# Revit family: Shower-Whitehall-BestCare-WH418-CSH
name_source: partatom
category: Plumbing Fixtures
revit_build: Autodesk Revit 2018 (Build: 20170223_1515(x64)
units: mm (PartAtom-declared; Revit-internal decimal feet)

## family parameters
Cut with Voids When Loaded = No
Host = Face
OmniClass Number = 23.45.05.14.17
OmniClass Title = Showers
Part Type = Normal
Room Calculation Point = No
Round Connector Dimension = Use Diameter
Shared = Yes

## types (1)
- WH418-CSH
    ADA Compliant = Yes
    Assembly Code = D2010710
    CW Connection = Yes
    CWFU = 3
    Cold Water Connection Diameter = 1/2"
    Cold Water Connection Radius = 1/4"
    Default Elevation = 72"
    Description = BestCare® Ligature-Resistant Flush Mount Shower
    Flow Rate = 1.5 GPM
    HW Connection = Yes
    HWFU = 3
    Height = 25"
    Hot Water Connection Diameter = 1/2"
    Hot Water Connection Radius = 1/4"
    IAPMO Compliance = Mixing Valve meets criteria for temperature and pressure changes,
defined by ASSE 1016. Valve conforms with lead free requirements of NSF61, Section 9, 1997 and CHSC 116875.
    Installation Type = Flush Mounted
    Manufacturer = Whitehall Mfg.
    Material = Stainless Steel-Whitehall-Powder Coated White
    Max. Working Pressure = 125 PSI
    Model = WH418-CSH
    Outlet Connection Diameter = 3/8"
    Panel Material = Stainless Steel-Whitehall-Powder Coated White
    Price = Prices may vary. Please consult Manufacturer Representative for most up-to-date price list.
    Product Documentation Link = https://www.whitehallmfg.com
    Product Page URL = https://www.whitehallmfg.com
    Revised Date = 04/19/2022
    Showerhead Material = Brass-Whitehall-Chrome Plated
    Tempered Water Connection = Yes
    Tri-Lever Handle Diameter = 5 1/2"
    URL = https://www.whitehallmfg.com
    Valve Material = Brass-Whitehall-Chrome Plated
    Vent Connection = No
    WFU = 4
    Waste Connection = No
    Width = 9"

## geometry (parser evidence)
native form markers: Sweep x3
no freeform markers — native parametric forms only
